# Revit family: CBCONFTYP002
name_source: partatom
category: Furniture
units: mm (PartAtom-declared; Revit-internal decimal feet)

## family parameters
Always vertical = Yes
Cut with Voids When Loaded = No
OmniClass Number = 23.40.20.00
OmniClass Title = General Furniture and Specialties
Render Appearance Source = Family Geometry
Room Calculation Point = No
Shared = No
Work Plane-Based = No

## types (1)
- CBCONFTYP002
    Cost = 30126 $
    Default Elevation = 0 mm  [stored 0 ft]
    Description = 10 x Natick Black Configurable Task Chair, 2 x LB LOUNGE, BACKLESS, 66 WIDTH CLOSED BOTTOM, 1 x CBX Buffet Bookcase 24D x 48W, 1 x Cbx Table Taper 60D X 168W 2Mm 4 Sec 4 A-Base, 1 x CBX Trash Bin 24D x 36W
    Exported From CET Designer = Yes
    Manufacturer = AIS
    Model = 4900C
    Show CBCONFTYP002 = Yes
    VisibilityIndex = 0

note: [stored X ft] marks values corroborated as IEEE doubles in the binary element streams (Revit-internal decimal feet)

## geometry (parser evidence)
native form markers: Sweep x3
no freeform markers — native parametric forms only
